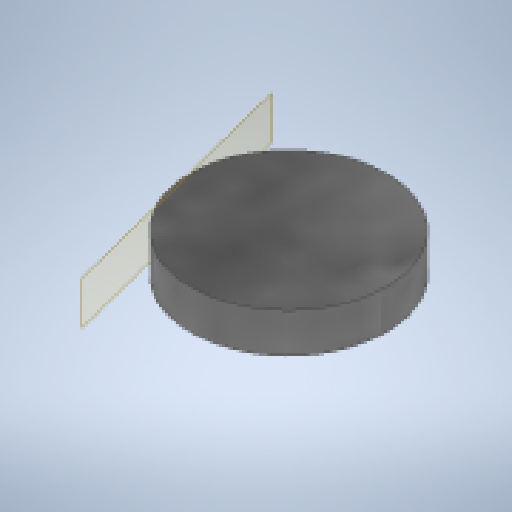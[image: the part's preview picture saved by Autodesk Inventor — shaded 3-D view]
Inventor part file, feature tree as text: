
AUTODESK INVENTOR PART (.ipt)
format: ipt  version: 2025.2 (Build 292293000, 293)  size: 160,256 bytes
history: native  units: mm
features: other x5, extrude x2, sketch x2
ambient origin geometry x8: Origin, YZ Plane, XZ Plane, XY Plane, X Axis, Y Axis, Z Axis, Center Point
bodies: Body1 (feature_tree)
feature tree (9):
  other  "ソリッド1"
  extrude  "押し出し1"  Depth=10.0mm
  other  "作業平面1"
  extrude  "押し出し2"  Depth=2.0mm TaperAngle=0.0deg
  sketch  "スケッチ1"
  sketch  "スケッチ2"
  other  "<userpath>\OneDrive\ドキュメント\New Controller\Hardware\Assembly.iam"
  other  "Assembly.iam"
  other  "Body_compleat01:1"
